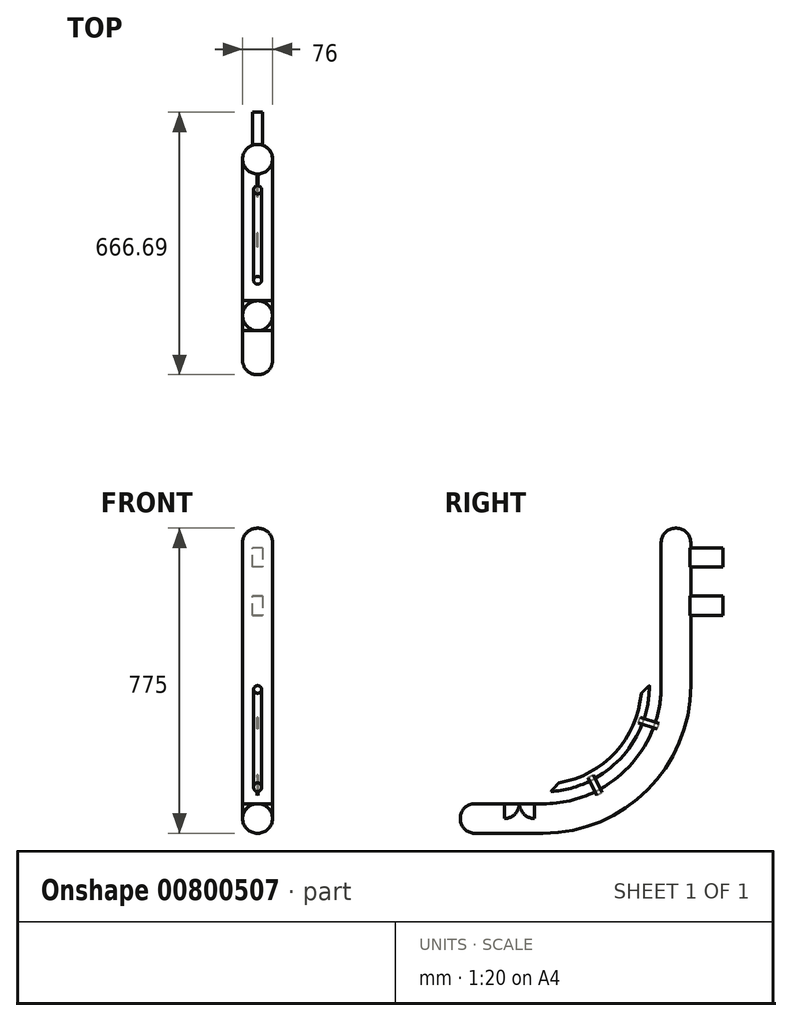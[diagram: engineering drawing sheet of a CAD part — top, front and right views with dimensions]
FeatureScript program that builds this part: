
annotation { "Feature Type Name" : "Feature", "Feature Type Description" : "" }
export const myFeature = defineFeature(function(context is Context, id is Id, definition is map)
    precondition{}
    {
        {
            var Q0;
            Q0=qCreatedBy(makeId("Right.planeOp"),FACE);
            var sketch = newSketch(context, id + "F0", { "sketchPlane" : qUnion([Q0])});
            skLineSegment(sketch, "E0", {"start": v(0, 0) * mm, "end": v(0, 563) * mm});
            skLineSegment(sketch, "E1", {"start": v(0, 563) * mm, "end": v(345, 563) * mm});
            skLineSegment(sketch, "E2", {"start": v(0, 563) * mm, "end": v(-345, 563) * mm});
            skLineSegment(sketch, "E3", {"start": v(0, 0) * mm, "end": v(38, 0) * mm});
            skLineSegment(sketch, "E4", {"start": v(38, 0) * mm, "end": v(345, 563) * mm});
            skSolve(sketch);
        }
        {
            var Q0;
            Q0=makeQuery(id+"F0.imprint","IMPRINT",FACE,{"disambiguationData":[TD([[makeQuery(id+"F0.imprint","IMPRINT",EDGE,{"derivedFrom":sQuery(id+"F0.wireOp",EDGE,"E0")}),-1.0]])]});
            var Q1;
            Q1=sQuery(id+"F0.wireOp",EDGE,"E0");
            revolve(context, id + "F1", {"surfaceOperationType" : NewSurfaceOperationType.NEW, "entities" : qUnion([Q0]), "axis" : qUnion([Q1]), "revolveType" : RevolveType.FULL});
        }
        {
            var Q0;
            Q0=qCreatedBy(makeId("Right.planeOp"),FACE);
            var sketch = newSketch(context, id + "F2", { "sketchPlane" : qUnion([Q0])});
            skLineSegment(sketch, "E5", {"start": v(345, 563) * mm, "end": v(38, 0) * mm});
            skLineSegment(sketch, "E6", {"start": v(-38, 0) * mm, "end": v(-345, 563) * mm});
            skPoint(sketch, "E7.visualSharp", {"position": v(395, 0) * mm});
            skArc(sketch, "E7.filletArc", {"start": v(60.16, 0) * mm, "mid": v(272.3, 87.87) * mm, "end": v(360.16, 300) * mm});
            skLineSegment(sketch, "E8", {"start": v(360.16, 700) * mm, "end": v(435.16, 700) * mm});
            skLineSegment(sketch, "E9", {"start": v(-150, -75) * mm, "end": v(-150, 0) * mm});
            skArc(sketch, "E10.0", {"start": v(60.16, -75) * mm, "mid": v(325.32, 34.83) * mm, "end": v(435.16, 300) * mm});
            skLineSegment(sketch, "E11", {"start": v(60.16, 0) * mm, "end": v(-150, 0) * mm});
            skLineSegment(sketch, "E12", {"start": v(360.16, 700) * mm, "end": v(360.16, 300) * mm});
            skLineSegment(sketch, "E13", {"start": v(435.16, 700) * mm, "end": v(435.16, 300) * mm});
            skLineSegment(sketch, "E14", {"start": v(60.16, -75) * mm, "end": v(-150, -75) * mm});
            skSolve(sketch);
        }
        {
            var Q0;
            {var subQ1=sQuery(id+"F2.wireOp",EDGE,"E7.filletArc");Q0=makeQuery(id+"F2.imprint","IMPRINT",FACE,{"disambiguationData":[TD([[makeQuery(id+"F2.imprint","IMPRINT",EDGE,{"derivedFrom":subQ1}),-1.0]])]});}
            extrude(context, id + "F3", {"entities" : qUnion([Q0]), "operationType" : NewBodyOperationType.ADD, "endBound" : BoundingType.SYMMETRIC, "oppositeDirection" : true, "depth" : 76 * mm, "offsetDistance" : 25.4 * mm});
        }
        {
            var Q0;
            Q0=makeQuery(id+"F3.opExtrude","CAP_EDGE",EDGE,{"disambiguationData":[OSD([sQuery(id+"F2.wireOp",EDGE,"E12")])],"isStart":false});
            var Q1;
            Q1=makeQuery(id+"F3.opExtrude","CAP_EDGE",EDGE,{"disambiguationData":[OSD([sQuery(id+"F2.wireOp",EDGE,"E12")])],"isStart":true});
            var Q2;
            Q2=makeQuery(id+"F3.opExtrude","CAP_EDGE",EDGE,{"disambiguationData":[OSD([sQuery(id+"F2.wireOp",EDGE,"E13")])],"isStart":true});
            var Q3;
            Q3=makeQuery(id+"F3.opExtrude","CAP_EDGE",EDGE,{"disambiguationData":[OSD([sQuery(id+"F2.wireOp",EDGE,"E13")])],"isStart":false});
            var Q4;
            Q4=makeQuery(id+"F3.opExtrude","CAP_EDGE",EDGE,{"disambiguationData":[OSD([sQuery(id+"F2.wireOp",EDGE,"E7.filletArc")])],"isStart":true});
            var Q5;
            Q5=makeQuery(id+"F3.opExtrude","CAP_EDGE",EDGE,{"disambiguationData":[OSD([sQuery(id+"F2.wireOp",EDGE,"E10.0")])],"isStart":true});
            var Q6;
            Q6=makeQuery(id+"F3.opExtrude","CAP_EDGE",EDGE,{"disambiguationData":[OSD([sQuery(id+"F2.wireOp",EDGE,"E14")])],"isStart":true});
            var Q7;
            {var subQ0=sQuery(id+"F2.wireOp",EDGE,"E9");var subQ1=sQuery(id+"F2.wireOp",EDGE,"E11");Q7=makeQuery(id+"F3.boolean.opBoolean","SPLIT",EDGE,{"disambiguationData":[TD([makeQuery(id+"F3.opExtrude","SWEPT_FACE",FACE,{"disambiguationData":[OSD([subQ0])]})])],"derivedFrom":makeQuery(id+"F3.opExtrude","CAP_EDGE",EDGE,{"disambiguationData":[OSD([subQ1])],"isStart":true})});}
            var Q8;
            {var subQ0=sQuery(id+"F2.wireOp",EDGE,"E7.filletArc");var subQ1=sQuery(id+"F2.wireOp",EDGE,"E11");Q8=makeQuery(id+"F3.boolean.opBoolean","SPLIT",EDGE,{"disambiguationData":[TD([makeQuery(id+"F3.opExtrude","SWEPT_FACE",FACE,{"disambiguationData":[OSD([subQ0])]})])],"derivedFrom":makeQuery(id+"F3.opExtrude","CAP_EDGE",EDGE,{"disambiguationData":[OSD([subQ1])],"isStart":true})});}
            var Q9;
            {var subQ0=sQuery(id+"F2.wireOp",EDGE,"E9");var subQ1=sQuery(id+"F2.wireOp",EDGE,"E11");Q9=makeQuery(id+"F3.boolean.opBoolean","SPLIT",EDGE,{"disambiguationData":[TD([makeQuery(id+"F3.opExtrude","SWEPT_FACE",FACE,{"disambiguationData":[OSD([subQ0])]})])],"derivedFrom":makeQuery(id+"F3.opExtrude","CAP_EDGE",EDGE,{"disambiguationData":[OSD([subQ1])],"isStart":false})});}
            var Q10;
            Q10=makeQuery(id+"F3.opExtrude","CAP_EDGE",EDGE,{"disambiguationData":[OSD([sQuery(id+"F2.wireOp",EDGE,"E14")])],"isStart":false});
            var Q11;
            Q11=makeQuery(id+"F3.opExtrude","CAP_EDGE",EDGE,{"disambiguationData":[OSD([sQuery(id+"F2.wireOp",EDGE,"E7.filletArc")])],"isStart":false});
            var Q12;
            {var subQ0=sQuery(id+"F2.wireOp",EDGE,"E7.filletArc");var subQ1=sQuery(id+"F2.wireOp",EDGE,"E11");Q12=makeQuery(id+"F3.boolean.opBoolean","SPLIT",EDGE,{"disambiguationData":[TD([makeQuery(id+"F3.opExtrude","SWEPT_FACE",FACE,{"disambiguationData":[OSD([subQ0])]})])],"derivedFrom":makeQuery(id+"F3.opExtrude","CAP_EDGE",EDGE,{"disambiguationData":[OSD([subQ1])],"isStart":false})});}
            var Q13;
            Q13=makeQuery(id+"F3.opExtrude","CAP_EDGE",EDGE,{"disambiguationData":[OSD([sQuery(id+"F2.wireOp",EDGE,"E10.0")])],"isStart":false});
            fillet(context, id + "F4", {"entities" : qUnion([Q0, Q1, Q2, Q3, Q4, Q5, Q6, Q7, Q8, Q9, Q10, Q11, Q12, Q13]), "radius" : 37.5 * mm, "tangentPropagation" : true, "allowEdgeOverflow" : false});
        }
        {
            var Q0;
            Q0=qCreatedBy(makeId("Right.planeOp"),FACE);
            var sketch = newSketch(context, id + "F5", { "sketchPlane" : qUnion([Q0])});
            skArc(sketch, "E15.0", {"start": v(60.16, 0) * mm, "mid": v(272.3, 87.87) * mm, "end": v(360.16, 300) * mm});
            skArc(sketch, "E16.0", {"start": v(80.15, 30.74) * mm, "mid": v(258.02, 116.28) * mm, "end": v(330.16, 300) * mm});
            skLineSegment(sketch, "E17", {"start": v(330.16, 300) * mm, "end": v(309.42, 280.76) * mm});
            skArc(sketch, "E18", {"start": v(80.15, 30.74) * mm, "mid": v(80.97, 30.79) * mm, "end": v(81.8, 30.87) * mm});
            skLineSegment(sketch, "E19", {"start": v(99.9, 53.18) * mm, "end": v(80.15, 30.74) * mm});
            skArc(sketch, "E20.trimOffspring", {"start": v(99.9, 53.18) * mm, "mid": v(244.08, 130.67) * mm, "end": v(309.42, 280.76) * mm});
            skSolve(sketch);
        }
        {
            var Q0;
            {var subQ1=sQuery(id+"F5.wireOp",EDGE,"E17");Q0=makeQuery(id+"F5.imprint","IMPRINT",FACE,{"disambiguationData":[TD([[makeQuery(id+"F5.imprint","IMPRINT",EDGE,{"derivedFrom":subQ1}),1.0]])]});}
            extrude(context, id + "F6", {"entities" : qUnion([Q0]), "endBound" : BoundingType.SYMMETRIC, "depth" : 20 * mm, "offsetDistance" : 25.4 * mm});
        }
        {
            var Q0;
            Q0=makeQuery(id+"F6.opExtrude","CAP_EDGE",EDGE,{"disambiguationData":[OSD([sQuery(id+"F5.wireOp",EDGE,"E20.trimOffspring")])],"isStart":true});
            var Q1;
            Q1=makeQuery(id+"F6.opExtrude","CAP_EDGE",EDGE,{"disambiguationData":[OSD([sQuery(id+"F5.wireOp",EDGE,"E20.trimOffspring")])],"isStart":false});
            var Q2;
            Q2=makeQuery(id+"F6.opExtrude","CAP_EDGE",EDGE,{"disambiguationData":[OSD([sQuery(id+"F5.wireOp",EDGE,"E16.0")])],"isStart":false});
            var Q3;
            Q3=makeQuery(id+"F6.opExtrude","CAP_EDGE",EDGE,{"disambiguationData":[OSD([sQuery(id+"F5.wireOp",EDGE,"E16.0")])],"isStart":true});
            fillet(context, id + "F7", {"entities" : qUnion([Q0, Q1, Q2, Q3]), "radius" : 9.8 * mm, "tangentPropagation" : true, "allowEdgeOverflow" : false});
        }
        {
            var Q0;
            Q0=qCreatedBy(makeId("Right.planeOp"),FACE);
            var sketch = newSketch(context, id + "F8", { "sketchPlane" : qUnion([Q0])});
            skLineSegment(sketch, "E21", {"start": v(174.17, 66.81) * mm, "end": v(196.33, 21.49) * mm});
            skLineSegment(sketch, "E22", {"start": v(306.97, 219.64) * mm, "end": v(354.95, 204.02) * mm});
            skArc(sketch, "E23", {"start": v(174.17, 66.81) * mm, "mid": v(180.87, 70.2) * mm, "end": v(187.46, 73.8) * mm});
            skArc(sketch, "E24", {"start": v(196.33, 21.49) * mm, "mid": v(203.03, 24.86) * mm, "end": v(209.65, 28.4) * mm});
            skArc(sketch, "E25.trimOffspring", {"start": v(349.96, 189.87) * mm, "mid": v(352.54, 196.91) * mm, "end": v(354.95, 204.02) * mm});
            skLineSegment(sketch, "E26.trimOffspring", {"start": v(187.46, 73.8) * mm, "end": v(209.65, 28.4) * mm});
            skArc(sketch, "E27.trimOffspring", {"start": v(301.92, 205.5) * mm, "mid": v(304.55, 212.54) * mm, "end": v(306.97, 219.64) * mm});
            skLineSegment(sketch, "E28.trimOffspring", {"start": v(301.92, 205.5) * mm, "end": v(349.96, 189.87) * mm});
            skSolve(sketch);
        }
        {
            var Q0;
            Q0=makeQuery(id+"F8.imprint","IMPRINT",FACE,{"disambiguationData":[TD([[makeQuery(id+"F8.imprint","IMPRINT",EDGE,{"derivedFrom":sQuery(id+"F8.wireOp",EDGE,"E22")}),-1.0]])]});
            var Q1;
            Q1=makeQuery(id+"F8.imprint","IMPRINT",FACE,{"disambiguationData":[TD([[makeQuery(id+"F8.imprint","IMPRINT",EDGE,{"derivedFrom":sQuery(id+"F8.wireOp",EDGE,"E21")}),1.0]])]});
            extrude(context, id + "F9", {"entities" : qUnion([Q0, Q1]), "endBound" : BoundingType.SYMMETRIC, "depth" : 3 * mm, "offsetDistance" : 25.4 * mm});
        }
        {
            var Q0;
            Q0=qCreatedBy(makeId("Right.planeOp"),FACE);
            var sketch = newSketch(context, id + "F10", { "sketchPlane" : qUnion([Q0])});
            skLineSegment(sketch, "E29.bottom", {"start": v(417.84, 650.28) * mm, "end": v(516.7, 650.28) * mm});
            skLineSegment(sketch, "E29.top", {"start": v(417.84, 601.46) * mm, "end": v(516.7, 601.46) * mm});
            skLineSegment(sketch, "E29.left", {"start": v(417.84, 650.28) * mm, "end": v(417.84, 601.46) * mm});
            skLineSegment(sketch, "E29.right", {"start": v(516.7, 650.28) * mm, "end": v(516.7, 601.46) * mm});
            skLineSegment(sketch, "E30.bottom", {"start": v(516.7, 527.43) * mm, "end": v(417.84, 527.43) * mm});
            skLineSegment(sketch, "E30.top", {"start": v(516.7, 478.61) * mm, "end": v(417.84, 478.61) * mm});
            skLineSegment(sketch, "E30.left", {"start": v(516.7, 527.43) * mm, "end": v(516.7, 478.61) * mm});
            skLineSegment(sketch, "E30.right", {"start": v(417.84, 527.43) * mm, "end": v(417.84, 478.61) * mm});
            skSolve(sketch);
        }
        {
            var Q0;
            Q0=makeQuery(id+"F10.imprint","IMPRINT",FACE,{"disambiguationData":[TD([[makeQuery(id+"F10.imprint","IMPRINT",EDGE,{"derivedFrom":sQuery(id+"F10.wireOp",EDGE,"E29.bottom")}),-1.0]])]});
            var Q1;
            Q1=makeQuery(id+"F10.imprint","IMPRINT",FACE,{"disambiguationData":[TD([[makeQuery(id+"F10.imprint","IMPRINT",EDGE,{"derivedFrom":sQuery(id+"F10.wireOp",EDGE,"E30.bottom")}),1.0]])]});
            extrude(context, id + "F11", {"entities" : qUnion([Q0, Q1]), "operationType" : NewBodyOperationType.ADD, "endBound" : BoundingType.SYMMETRIC, "depth" : 25.4 * mm, "offsetDistance" : 25.4 * mm});
        }
        {
            var Q0;
            Q0=makeQuery(id+"F3.opExtrude","SWEPT_FACE",FACE,{"disambiguationData":[OSD([sQuery(id+"F2.wireOp",EDGE,"E9")])]});
            var Q1;
            Q1=makeQuery(id+"F3.opExtrude","SWEPT_FACE",FACE,{"disambiguationData":[OSD([sQuery(id+"F2.wireOp",EDGE,"E8")])]});
            fillet(context, id + "F12", {"entities" : qUnion([Q0, Q1]), "radius" : 36.18 * mm, "tangentPropagation" : true, "allowEdgeOverflow" : false});
        }
        {
            var Q0;
            Q0=qCreatedBy(makeId("Right.planeOp"),FACE);
            var sketch = newSketch(context, id + "F13", { "sketchPlane" : qUnion([Q0])});
            skLineSegment(sketch, "E31", {"start": v(0, 0) * mm, "end": v(0, 571.09) * mm});
            skLineSegment(sketch, "E32", {"start": v(0, 571.09) * mm, "end": v(352, 571.09) * mm});
            skLineSegment(sketch, "E33", {"start": v(352, 571.09) * mm, "end": v(307.67, 474.07) * mm});
            skLineSegment(sketch, "E34", {"start": v(307.67, 474.07) * mm, "end": v(42.18, 0) * mm});
            skLineSegment(sketch, "E35", {"start": v(42.18, 0) * mm, "end": v(0, 0) * mm});
            skSolve(sketch);
        }
        {
            var Q0;
            Q0=makeQuery(id+"F13.imprint","IMPRINT",FACE,{"disambiguationData":[TD([[makeQuery(id+"F13.imprint","IMPRINT",EDGE,{"derivedFrom":sQuery(id+"F13.wireOp",EDGE,"E31")}),-1.0]])]});
            var Q1;
            Q1=sQuery(id+"F13.wireOp",EDGE,"E31");
            revolve(context, id + "F14", {"operationType" : NewBodyOperationType.REMOVE, "surfaceOperationType" : NewSurfaceOperationType.NEW, "entities" : qUnion([Q0]), "axis" : qUnion([Q1]), "revolveType" : RevolveType.FULL, "oppositeDirection" : true});
        }
    });
